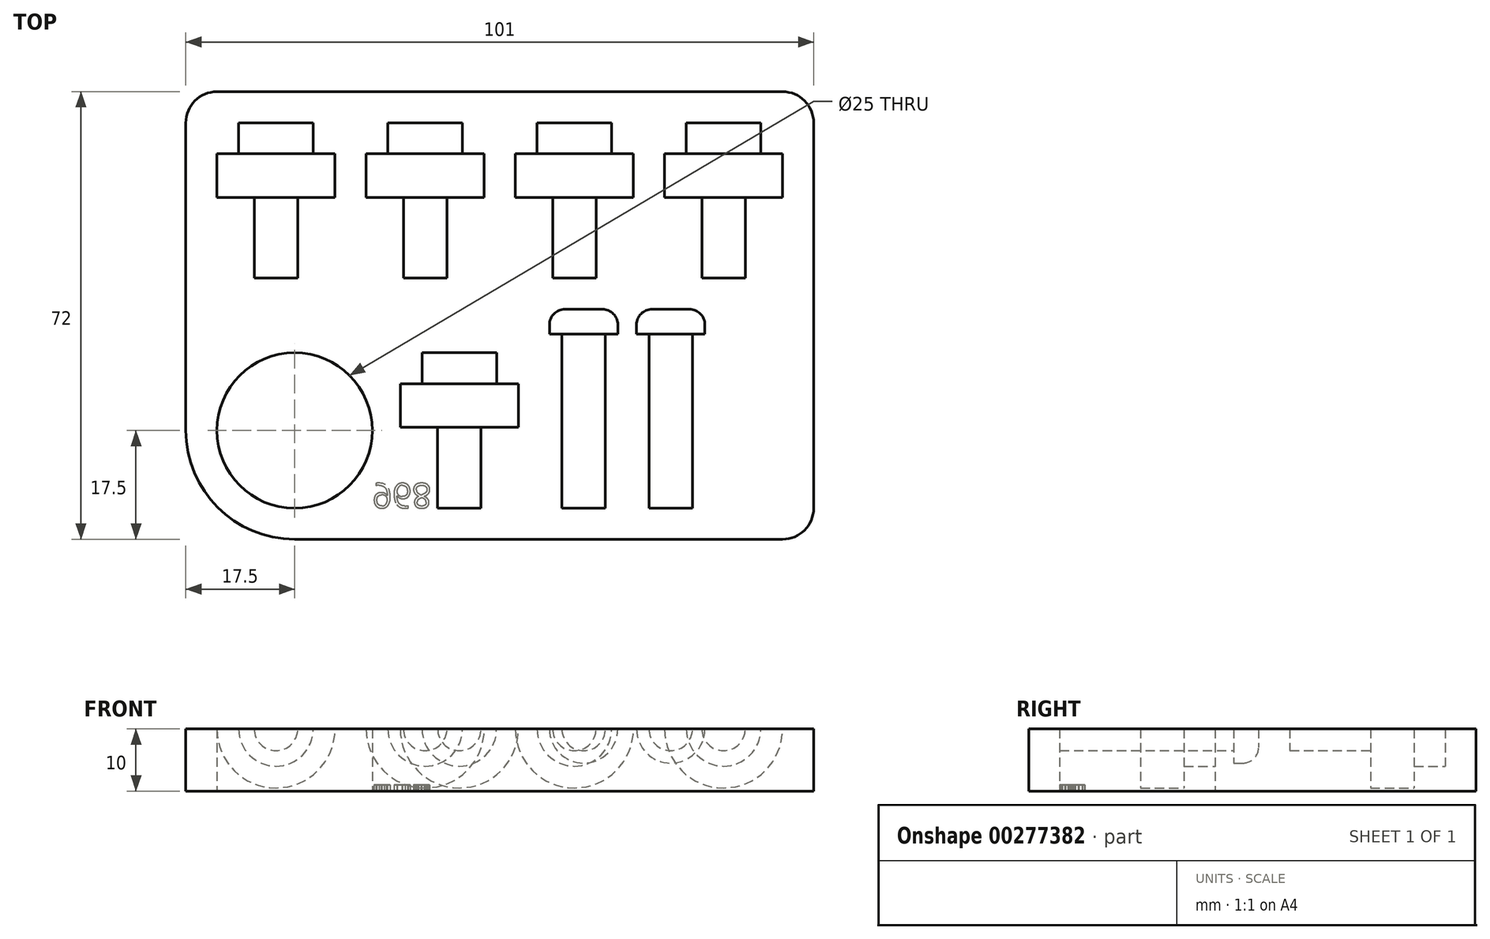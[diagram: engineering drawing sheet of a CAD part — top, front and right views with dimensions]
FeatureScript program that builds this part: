
annotation { "Feature Type Name" : "Feature", "Feature Type Description" : "" }
export const myFeature = defineFeature(function(context is Context, id is Id, definition is map)
    precondition{}
    {
        {
            var Q0;
            Q0=qCreatedBy(makeId("Top.planeOp"),FACE);
            var sketch = newSketch(context, id + "F0", { "sketchPlane" : qUnion([Q0])});
            skLineSegment(sketch, "E0.bottom", {"start": v(17.5, 0) * mm, "end": v(96, 0) * mm});
            skLineSegment(sketch, "E0.top", {"start": v(5, 72) * mm, "end": v(96, 72) * mm});
            skLineSegment(sketch, "E0.left", {"start": v(0, 17.5) * mm, "end": v(0, 67) * mm});
            skLineSegment(sketch, "E0.right", {"start": v(101, 5) * mm, "end": v(101, 67) * mm});
            skLineSegment(sketch, "E1.bottom", {"start": v(0, 0) * mm, "end": v(17.5, 0) * mm, "construction": true});
            skLineSegment(sketch, "E1.top", {"start": v(0, 17.5) * mm, "end": v(17.5, 17.5) * mm, "construction": true});
            skLineSegment(sketch, "E1.left", {"start": v(0, 0) * mm, "end": v(0, 17.5) * mm, "construction": true});
            skLineSegment(sketch, "E1.right", {"start": v(17.5, 0) * mm, "end": v(17.5, 17.5) * mm, "construction": true});
            skCircle(sketch, "E2", {"center": v(17.5, 17.5) * mm, "radius": 12.5 * mm});
            skPoint(sketch, "E3.visualSharp", {"position": v(0, 0) * mm});
            skArc(sketch, "E3.filletArc", {"start": v(0, 17.5) * mm, "mid": v(5.13, 5.13) * mm, "end": v(17.5, 0) * mm});
            skPoint(sketch, "E4.visualSharp", {"position": v(0, 72) * mm});
            skArc(sketch, "E4.filletArc", {"start": v(5, 72) * mm, "mid": v(1.46, 70.54) * mm, "end": v(0, 67) * mm});
            skPoint(sketch, "E5.visualSharp", {"position": v(101, 72) * mm});
            skArc(sketch, "E5.filletArc", {"start": v(101, 67) * mm, "mid": v(99.54, 70.54) * mm, "end": v(96, 72) * mm});
            skPoint(sketch, "E6.visualSharp", {"position": v(101, 0) * mm});
            skArc(sketch, "E6.filletArc", {"start": v(96, 0) * mm, "mid": v(99.54, 1.46) * mm, "end": v(101, 5) * mm});
            skSolve(sketch);
        }
        {
            var Q0;
            Q0=makeQuery(id+"F0.imprint","IMPRINT",FACE,{"disambiguationData":[TD([[makeQuery(id+"F0.imprint","IMPRINT",EDGE,{"derivedFrom":sQuery(id+"F0.wireOp",EDGE,"E0.bottom")}),1.0]])]});
            extrude(context, id + "F1", {"entities" : qUnion([Q0]), "depth" : 10 * mm});
        }
        {
            var Q0;
            Q0=makeQuery(id+"F1.opExtrude","CAP_FACE",FACE,{"disambiguationData":[OSD([sQuery(id+"F0.wireOp",EDGE,"E0.bottom"),sQuery(id+"F0.wireOp",EDGE,"E0.top"),sQuery(id+"F0.wireOp",EDGE,"E0.right"),sQuery(id+"F0.wireOp",EDGE,"E2"),sQuery(id+"F0.wireOp",EDGE,"E3.filletArc"),sQuery(id+"F0.wireOp",EDGE,"E4.filletArc"),sQuery(id+"F0.wireOp",EDGE,"E5.filletArc"),sQuery(id+"F0.wireOp",EDGE,"E6.filletArc")])],"isStart":false});
            var sketch = newSketch(context, id + "F2", { "sketchPlane" : qUnion([Q0])});
            skLineSegment(sketch, "E7.bottom", {"start": v(0, 0) * mm, "end": v(44, 0) * mm, "construction": true});
            skLineSegment(sketch, "E7.top", {"start": v(0, 5) * mm, "end": v(44, 5) * mm, "construction": true});
            skLineSegment(sketch, "E7.left", {"start": v(0, 0) * mm, "end": v(0, 5) * mm, "construction": true});
            skLineSegment(sketch, "E7.right", {"start": v(44, 0) * mm, "end": v(44, 5) * mm, "construction": true});
            skLineSegment(sketch, "E8.bottom", {"start": v(44, 5) * mm, "end": v(47.5, 5) * mm});
            skLineSegment(sketch, "E8.left", {"start": v(44, 5) * mm, "end": v(44, 18) * mm});
            skLineSegment(sketch, "E8.right", {"start": v(47.5, 5) * mm, "end": v(47.5, 18) * mm});
            skLineSegment(sketch, "E9.bottom", {"start": v(47.5, 18) * mm, "end": v(53.5, 18) * mm});
            skLineSegment(sketch, "E9.top", {"start": v(50, 25) * mm, "end": v(53.5, 25) * mm});
            skLineSegment(sketch, "E9.left", {"start": v(44, 18) * mm, "end": v(44, 25) * mm});
            skLineSegment(sketch, "E9.right", {"start": v(53.5, 18) * mm, "end": v(53.5, 25) * mm});
            skLineSegment(sketch, "E10.top", {"start": v(44, 30) * mm, "end": v(50, 30) * mm});
            skLineSegment(sketch, "E10.left", {"start": v(44, 25) * mm, "end": v(44, 30) * mm});
            skLineSegment(sketch, "E10.right", {"start": v(50, 25) * mm, "end": v(50, 30) * mm});
            skLineSegment(sketch, "E11", {"start": v(44, 5) * mm, "end": v(64, 5) * mm, "construction": true});
            skLineSegment(sketch, "E12", {"start": v(64, 5) * mm, "end": v(78, 5) * mm, "construction": true});
            skLineSegment(sketch, "E13", {"start": v(38.5, 42) * mm, "end": v(62.5, 42) * mm, "construction": true});
            skLineSegment(sketch, "E14", {"start": v(62.5, 42) * mm, "end": v(86.5, 42) * mm, "construction": true});
            skLineSegment(sketch, "E15.bottom", {"start": v(86.5, 42) * mm, "end": v(90, 42) * mm});
            skLineSegment(sketch, "E15.left", {"start": v(86.5, 42) * mm, "end": v(86.5, 55) * mm});
            skLineSegment(sketch, "E15.right", {"start": v(90, 42) * mm, "end": v(90, 55) * mm});
            skLineSegment(sketch, "E16.bottom", {"start": v(90, 55) * mm, "end": v(96, 55) * mm});
            skLineSegment(sketch, "E16.top", {"start": v(92.5, 62) * mm, "end": v(96, 62) * mm});
            skLineSegment(sketch, "E16.left", {"start": v(86.5, 55) * mm, "end": v(86.5, 62) * mm});
            skLineSegment(sketch, "E16.right", {"start": v(96, 55) * mm, "end": v(96, 62) * mm});
            skLineSegment(sketch, "E17.top", {"start": v(86.5, 67) * mm, "end": v(92.5, 67) * mm});
            skLineSegment(sketch, "E17.left", {"start": v(86.5, 62) * mm, "end": v(86.5, 67) * mm});
            skLineSegment(sketch, "E17.right", {"start": v(92.5, 62) * mm, "end": v(92.5, 67) * mm});
            skLineSegment(sketch, "E18.bottom", {"start": v(62.5, 42) * mm, "end": v(66, 42) * mm});
            skLineSegment(sketch, "E18.left", {"start": v(62.5, 42) * mm, "end": v(62.5, 55) * mm});
            skLineSegment(sketch, "E18.right", {"start": v(66, 42) * mm, "end": v(66, 55) * mm});
            skLineSegment(sketch, "E19.bottom", {"start": v(66, 55) * mm, "end": v(72, 55) * mm});
            skLineSegment(sketch, "E19.top", {"start": v(68.5, 62) * mm, "end": v(72, 62) * mm});
            skLineSegment(sketch, "E19.left", {"start": v(62.5, 55) * mm, "end": v(62.5, 62) * mm});
            skLineSegment(sketch, "E19.right", {"start": v(72, 55) * mm, "end": v(72, 62) * mm});
            skLineSegment(sketch, "E20.top", {"start": v(62.5, 67) * mm, "end": v(68.5, 67) * mm});
            skLineSegment(sketch, "E20.left", {"start": v(62.5, 62) * mm, "end": v(62.5, 67) * mm});
            skLineSegment(sketch, "E20.right", {"start": v(68.5, 62) * mm, "end": v(68.5, 67) * mm});
            skLineSegment(sketch, "E21.bottom", {"start": v(38.5, 42) * mm, "end": v(42, 42) * mm});
            skLineSegment(sketch, "E21.left", {"start": v(38.5, 42) * mm, "end": v(38.5, 55) * mm});
            skLineSegment(sketch, "E21.right", {"start": v(42, 42) * mm, "end": v(42, 55) * mm});
            skLineSegment(sketch, "E22.bottom", {"start": v(42, 55) * mm, "end": v(48, 55) * mm});
            skLineSegment(sketch, "E22.top", {"start": v(44.5, 62) * mm, "end": v(48, 62) * mm});
            skLineSegment(sketch, "E22.left", {"start": v(38.5, 55) * mm, "end": v(38.5, 62) * mm});
            skLineSegment(sketch, "E22.right", {"start": v(48, 55) * mm, "end": v(48, 62) * mm});
            skLineSegment(sketch, "E23.top", {"start": v(38.5, 67) * mm, "end": v(44.5, 67) * mm});
            skLineSegment(sketch, "E23.left", {"start": v(38.5, 62) * mm, "end": v(38.5, 67) * mm});
            skLineSegment(sketch, "E23.right", {"start": v(44.5, 62) * mm, "end": v(44.5, 67) * mm});
            skLineSegment(sketch, "E24.bottom", {"start": v(64, 5) * mm, "end": v(67.5, 5) * mm});
            skLineSegment(sketch, "E24.left", {"start": v(64, 5) * mm, "end": v(64, 33) * mm});
            skLineSegment(sketch, "E24.right", {"start": v(67.5, 5) * mm, "end": v(67.5, 33) * mm});
            skLineSegment(sketch, "E25.bottom", {"start": v(67.5, 33) * mm, "end": v(69.5, 33) * mm});
            skLineSegment(sketch, "E25.top", {"start": v(64, 37) * mm, "end": v(67, 37) * mm});
            skLineSegment(sketch, "E25.left", {"start": v(64, 33) * mm, "end": v(64, 37) * mm});
            skLineSegment(sketch, "E25.right", {"start": v(69.5, 33) * mm, "end": v(69.5, 34.5) * mm});
            skPoint(sketch, "E26.visualSharp", {"position": v(69.5, 37) * mm});
            skArc(sketch, "E26.filletArc", {"start": v(69.5, 34.5) * mm, "mid": v(68.77, 36.27) * mm, "end": v(67, 37) * mm});
            skLineSegment(sketch, "E27.bottom", {"start": v(78, 5) * mm, "end": v(81.5, 5) * mm});
            skLineSegment(sketch, "E27.left", {"start": v(78, 5) * mm, "end": v(78, 33) * mm});
            skLineSegment(sketch, "E27.right", {"start": v(81.5, 5) * mm, "end": v(81.5, 33) * mm});
            skLineSegment(sketch, "E28.bottom", {"start": v(81.5, 33) * mm, "end": v(83.5, 33) * mm});
            skLineSegment(sketch, "E28.top", {"start": v(78, 37) * mm, "end": v(81, 37) * mm});
            skLineSegment(sketch, "E28.left", {"start": v(78, 33) * mm, "end": v(78, 37) * mm});
            skLineSegment(sketch, "E28.right", {"start": v(83.5, 33) * mm, "end": v(83.5, 34.5) * mm});
            skPoint(sketch, "E29.visualSharp", {"position": v(83.5, 37) * mm});
            skArc(sketch, "E29.filletArc", {"start": v(83.5, 34.5) * mm, "mid": v(82.77, 36.27) * mm, "end": v(81, 37) * mm});
            skLineSegment(sketch, "E30", {"start": v(38.5, 42) * mm, "end": v(14.5, 42) * mm, "construction": true});
            skLineSegment(sketch, "E31.bottom", {"start": v(14.5, 42) * mm, "end": v(18, 42) * mm});
            skLineSegment(sketch, "E31.left", {"start": v(14.5, 42) * mm, "end": v(14.5, 55) * mm});
            skLineSegment(sketch, "E31.right", {"start": v(18, 42) * mm, "end": v(18, 55) * mm});
            skLineSegment(sketch, "E32.bottom", {"start": v(18, 55) * mm, "end": v(24, 55) * mm});
            skLineSegment(sketch, "E32.top", {"start": v(20.5, 62) * mm, "end": v(24, 62) * mm});
            skLineSegment(sketch, "E32.left", {"start": v(14.5, 55) * mm, "end": v(14.5, 62) * mm});
            skLineSegment(sketch, "E32.right", {"start": v(24, 55) * mm, "end": v(24, 62) * mm});
            skLineSegment(sketch, "E33.top", {"start": v(14.5, 67) * mm, "end": v(20.5, 67) * mm});
            skLineSegment(sketch, "E33.left", {"start": v(14.5, 62) * mm, "end": v(14.5, 67) * mm});
            skLineSegment(sketch, "E33.right", {"start": v(20.5, 62) * mm, "end": v(20.5, 67) * mm});
            skSolve(sketch);
        }
        {
            var Q0;
            Q0=makeQuery(id+"F2.imprint","IMPRINT",FACE,{"disambiguationData":[TD([[makeQuery(id+"F2.imprint","IMPRINT",EDGE,{"derivedFrom":sQuery(id+"F2.wireOp",EDGE,"E21.bottom")}),1.0]])]});
            var Q1;
            Q1=sQuery(id+"F2.wireOp",EDGE,"E21.left");
            revolve(context, id + "F3", {"operationType" : NewBodyOperationType.REMOVE, "entities" : qUnion([Q0]), "axis" : qUnion([Q1]), "revolveType" : RevolveType.FULL, "oppositeDirection" : true});
        }
        {
            var Q0;
            Q0=makeQuery(id+"F2.imprint","IMPRINT",FACE,{"disambiguationData":[TD([[makeQuery(id+"F2.imprint","IMPRINT",EDGE,{"derivedFrom":sQuery(id+"F2.wireOp",EDGE,"E31.bottom")}),1.0]])]});
            var Q1;
            Q1=sQuery(id+"F2.wireOp",EDGE,"E31.left");
            revolve(context, id + "F4", {"operationType" : NewBodyOperationType.REMOVE, "entities" : qUnion([Q0]), "axis" : qUnion([Q1]), "revolveType" : RevolveType.FULL, "oppositeDirection" : true});
        }
        {
            var Q0;
            Q0=makeQuery(id+"F2.imprint","IMPRINT",FACE,{"disambiguationData":[TD([[makeQuery(id+"F2.imprint","IMPRINT",EDGE,{"derivedFrom":sQuery(id+"F2.wireOp",EDGE,"E18.bottom")}),1.0]])]});
            var Q1;
            Q1=sQuery(id+"F2.wireOp",EDGE,"E18.left");
            revolve(context, id + "F5", {"operationType" : NewBodyOperationType.REMOVE, "entities" : qUnion([Q0]), "axis" : qUnion([Q1]), "revolveType" : RevolveType.FULL, "oppositeDirection" : true});
        }
        {
            var Q0;
            Q0=makeQuery(id+"F2.imprint","IMPRINT",FACE,{"disambiguationData":[TD([[makeQuery(id+"F2.imprint","IMPRINT",EDGE,{"derivedFrom":sQuery(id+"F2.wireOp",EDGE,"E24.bottom")}),1.0]])]});
            var Q1;
            Q1=sQuery(id+"F2.wireOp",EDGE,"E24.left");
            revolve(context, id + "F6", {"operationType" : NewBodyOperationType.REMOVE, "entities" : qUnion([Q0]), "axis" : qUnion([Q1]), "revolveType" : RevolveType.FULL, "oppositeDirection" : true});
        }
        {
            var Q0;
            Q0=makeQuery(id+"F2.imprint","IMPRINT",FACE,{"disambiguationData":[TD([[makeQuery(id+"F2.imprint","IMPRINT",EDGE,{"derivedFrom":sQuery(id+"F2.wireOp",EDGE,"E27.bottom")}),1.0]])]});
            var Q1;
            Q1=sQuery(id+"F2.wireOp",EDGE,"E27.left");
            revolve(context, id + "F7", {"operationType" : NewBodyOperationType.REMOVE, "entities" : qUnion([Q0]), "axis" : qUnion([Q1]), "revolveType" : RevolveType.FULL, "oppositeDirection" : true});
        }
        {
            var Q0;
            Q0=makeQuery(id+"F2.imprint","IMPRINT",FACE,{"disambiguationData":[TD([[makeQuery(id+"F2.imprint","IMPRINT",EDGE,{"derivedFrom":sQuery(id+"F2.wireOp",EDGE,"E15.bottom")}),1.0]])]});
            var Q1;
            Q1=sQuery(id+"F2.wireOp",EDGE,"E15.left");
            revolve(context, id + "F8", {"operationType" : NewBodyOperationType.REMOVE, "entities" : qUnion([Q0]), "axis" : qUnion([Q1]), "revolveType" : RevolveType.FULL, "oppositeDirection" : true});
        }
        {
            var Q0;
            Q0=makeQuery(id+"F2.imprint","IMPRINT",FACE,{"disambiguationData":[TD([[makeQuery(id+"F2.imprint","IMPRINT",EDGE,{"derivedFrom":sQuery(id+"F2.wireOp",EDGE,"E8.bottom")}),1.0]])]});
            var Q1;
            Q1=sQuery(id+"F2.wireOp",EDGE,"E8.left");
            revolve(context, id + "F9", {"operationType" : NewBodyOperationType.REMOVE, "entities" : qUnion([Q0]), "axis" : qUnion([Q1]), "revolveType" : RevolveType.FULL, "oppositeDirection" : true});
        }
        {
            var Q0;
            Q0=makeQuery(id+"F1.opExtrude","CAP_FACE",FACE,{"disambiguationData":[OSD([sQuery(id+"F0.wireOp",EDGE,"E0.bottom"),sQuery(id+"F0.wireOp",EDGE,"E0.top"),sQuery(id+"F0.wireOp",EDGE,"E0.left"),sQuery(id+"F0.wireOp",EDGE,"E0.right"),sQuery(id+"F0.wireOp",EDGE,"E2"),sQuery(id+"F0.wireOp",EDGE,"E3.filletArc"),sQuery(id+"F0.wireOp",EDGE,"E4.filletArc"),sQuery(id+"F0.wireOp",EDGE,"E5.filletArc"),sQuery(id+"F0.wireOp",EDGE,"E6.filletArc")])],"isStart":true});
            var sketch = newSketch(context, id + "F10", { "sketchPlane" : qUnion([Q0])});
            skLineSegment(sketch, "E34.bottom", {"start": v(0, 0) * mm, "end": v(30, 0) * mm, "construction": true});
            skLineSegment(sketch, "E34.top", {"start": v(0, -5) * mm, "end": v(30, -5) * mm, "construction": true});
            skLineSegment(sketch, "E34.left", {"start": v(0, 0) * mm, "end": v(0, -5) * mm, "construction": true});
            skLineSegment(sketch, "E34.right", {"start": v(30, 0) * mm, "end": v(30, -5) * mm, "construction": true});
            skText(sketch, "E35", { "text": "968", "fontName": "OpenSans-Regular.ttf"});
            const initialGuessF10  = {"E35": [0.03, -0.009, 1, 0, 0.004]};
            skSetInitialGuess(sketch, initialGuessF10);
            skSolve(sketch);
        }
        {
            var Q0;
            Q0 = qSketchRegion(id + "F10", true);
            extrude(context, id + "F11", {"entities" : qUnion([Q0]), "operationType" : NewBodyOperationType.REMOVE, "oppositeDirection" : true, "depth" : 1 * mm});
        }
    });
